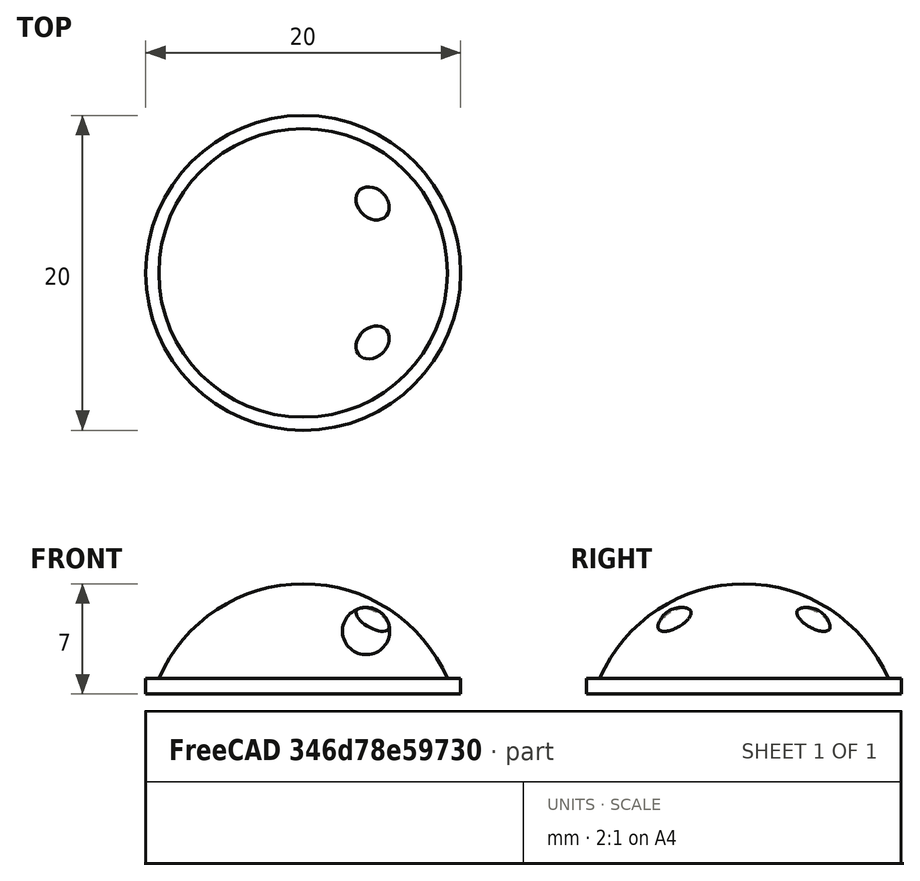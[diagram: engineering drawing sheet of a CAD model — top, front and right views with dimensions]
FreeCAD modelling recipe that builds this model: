
FCSTD DOCUMENT  (FreeCAD 0.16R6707 (Git))
Label: Cabeza_Androide
License: CreativeCommons Attribution-ShareAlike
LicenseURL: http://creativecommons.org/licenses/by-sa/4.0/
objects: Part::Sphere×3, Part::MultiFuse×3, Part::Cylinder×1
note: 7 computed .brp shape members not serialized (recipe doc carries the construction recipe); baked Part::Feature solids carry a one-line shape summary decoded from their .brp

FEATURE [Part::Sphere] Sphere  label="Casco"
  Angle1 = 20
  Angle2 = 90
  Angle3 = 360
  Placement = pos=(0,0,-3) rot=(0,0,1;0rad)
  Radius = 10
FEATURE [Part::Cylinder] Cylinder  label="Base"
  Angle = 360
  Height = 1
  Radius = 10
FEATURE [Part::MultiFuse] Fusion  label="Cabeza"
  Shapes = -> [Cylinder,Sphere]
FEATURE [Part::Sphere] Sphere001  label="Ojo"
  Angle1 = -90
  Angle2 = 90
  Angle3 = 360
  Placement = pos=(4,-4,4) rot=(0,0,1;0rad)
  Radius = 1.5
FEATURE [Part::Sphere] Sphere002  label="ojo2"
  Angle1 = -90
  Angle2 = 90
  Angle3 = 360
  Placement = pos=(4,4,4) rot=(0,0,1;0rad)
  Radius = 1.5
FEATURE [Part::MultiFuse] Fusion001  label="Ojos"
  Shapes = -> [Sphere001,Sphere002]
FEATURE [Part::MultiFuse] Fusion002  label="Cabeza_Android"
  Shapes = -> [Fusion,Fusion001]
